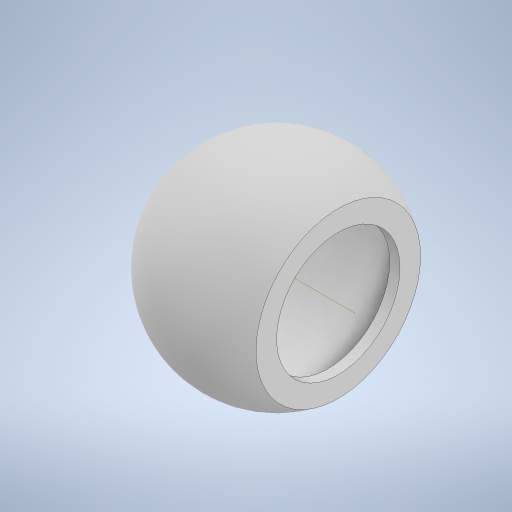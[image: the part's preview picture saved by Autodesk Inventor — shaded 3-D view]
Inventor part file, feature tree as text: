
AUTODESK INVENTOR PART (.ipt)
format: ipt  version: 2024.2 (Build 282272000, 272)  size: 304,128 bytes
history: native  units: mm
features: revolve x1, sketch x1
ambient origin geometry x8: Origin, YZ Plane, XZ Plane, XY Plane, X Axis, Y Axis, Z Axis, Center Point
bodies: Solid1 (feature_tree)
feature tree (2):
  revolve  "Revolution1"  [1 undecoded]
  sketch  "Sketch1"  dims[d1=10.0mm d5=4.0mm d6=1.0mm d7=0.5mm d8=0.8mm d9=8.0mm d10=0.451374mm d11=90.0deg]
note: 1 required parameter value undecoded (feature->parameter linkage not recoverable at this tier; creation-order binding heuristic only, values carry confidence <= 0.55)
